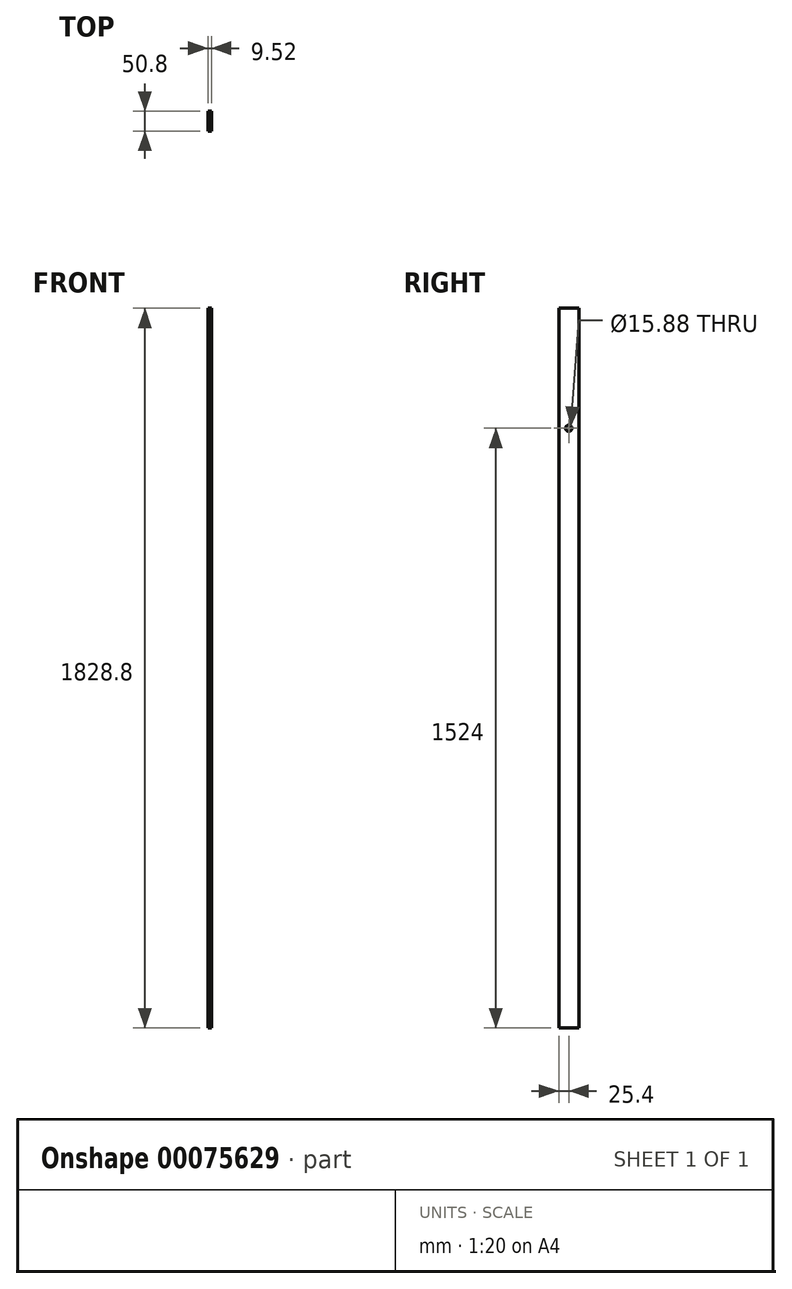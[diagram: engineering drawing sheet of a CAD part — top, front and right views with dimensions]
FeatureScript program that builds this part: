
annotation { "Feature Type Name" : "Feature", "Feature Type Description" : "" }
export const myFeature = defineFeature(function(context is Context, id is Id, definition is map)
    precondition{}
    {
        {
            var Q0;
            Q0=qCreatedBy(makeId("Top.planeOp"),FACE);
            var sketch = newSketch(context, id + "F0", { "sketchPlane" : qUnion([Q0])});
            skLineSegment(sketch, "E0.rect.bottom", {"start": v(4.76, 25.4) * mm, "end": v(-4.76, 25.4) * mm});
            skLineSegment(sketch, "E0.rect.top", {"start": v(4.76, -25.4) * mm, "end": v(-4.76, -25.4) * mm});
            skLineSegment(sketch, "E0.rect.left", {"start": v(4.76, 25.4) * mm, "end": v(4.76, -25.4) * mm});
            skLineSegment(sketch, "E0.rect.right", {"start": v(-4.76, 25.4) * mm, "end": v(-4.76, -25.4) * mm});
            skPoint(sketch, "E0.rect.middle", {"position": v(0, 0) * mm});
            skSolve(sketch);
        }
        {
            var Q0;
            Q0 = qSketchRegion(id + "F0", true);
            extrude(context, id + "F1", {"entities" : qUnion([Q0]), "endBound" : BoundingType.SYMMETRIC, "depth" : 1828.8 * mm});
        }
        {
            var Q0;
            Q0=makeQuery(id+"F1.opExtrude","SWEPT_FACE",FACE,{"disambiguationData":[OSD([sQuery(id+"F0.wireOp",EDGE,"E0.rect.left")])]});
            var sketch = newSketch(context, id + "F2", { "sketchPlane" : qUnion([Q0])});
            skCircle(sketch, "E1", {"center": v(0, 609.6) * mm, "radius": 7.94 * mm});
            skSolve(sketch);
        }
        {
            var Q0;
            Q0 = qSketchRegion(id + "F2", true);
            extrude(context, id + "F3", {"entities" : qUnion([Q0]), "operationType" : NewBodyOperationType.REMOVE, "endBound" : BoundingType.THROUGH_ALL, "oppositeDirection" : true, "depth" : 25.4 * mm});
        }
    });
